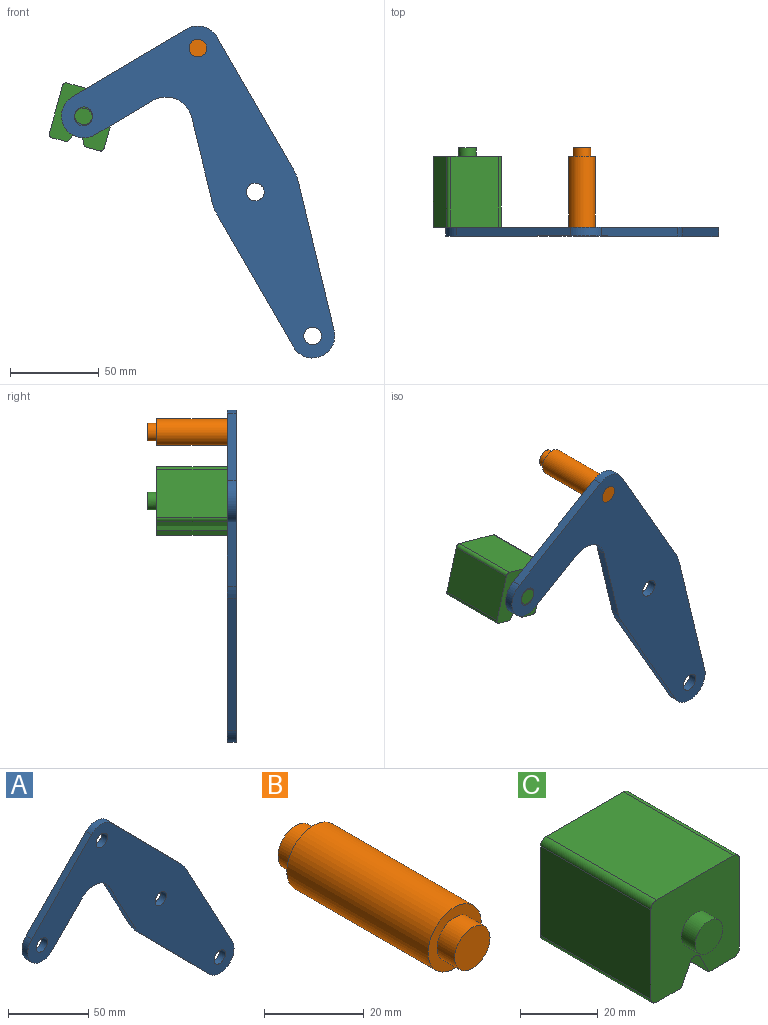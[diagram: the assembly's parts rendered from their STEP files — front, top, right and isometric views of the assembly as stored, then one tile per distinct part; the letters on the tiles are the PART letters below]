
ASSEMBLY  parts=3 mates=1
PART A: 18 faces, bbox 181.7x5x165.8 mm
  f0: plane 43.49x23.35mm, normal (-0.88,0,-0.47), area 246.8mm2, adj f1,f14,f16,f17
  f1: cylinder r=25mm len=5.75mm, axis (0,1,0), area 35.8mm2, adj f0,f2,f16,f17
  f2: plane 61.6x60.87mm, normal (-0.71,0,-0.7), area 433mm2, adj f1,f3,f16,f17
  f3: cylinder r=12.5mm len=21.39mm, axis (0,1,0), area 178.4mm2, adj f2,f4,f16,f17
  f4: plane 76.3x40.96mm, normal (0.88,0,0.47), area 433mm2, adj f3,f5,f16,f17
  f5: cylinder r=25mm len=5.75mm, axis (0,1,0), area 35.8mm2, adj f4,f6,f16,f17
  f6: plane 61.6x60.87mm, normal (0.71,0,0.7), area 433mm2, adj f5,f7,f16,f17
  f7: cylinder r=12.5mm len=17.78mm, axis (0,1,0), area 98.9mm2, adj f6,f8,f16,f17
  f8: plane 53.35x52.71mm, normal (-0.71,0,0.7), area 375mm2, adj f7,f9,f16,f17
  f9: cylinder r=12.5mm len=21.39mm, axis (0,1,0), area 196.3mm2, adj f8,f10,f16,f17
  f10: plane 26.86x26.54mm, normal (0.71,0,-0.7), area 188.8mm2, adj f9,f14,f16,f17
  f11: cylinder r=5mm len=10mm, axis (0,1,0), area 157.1mm2, adj f16,f17
  f12: cylinder r=5mm len=10mm, axis (0,1,0), area 157.1mm2, adj f16,f17
  f13: cylinder r=5mm len=10mm, axis (0,1,0), area 157.1mm2, adj f16,f17
  f14: cylinder r=15mm len=23.89mm, axis (0,1,0), area 140.2mm2, adj f0,f10,f16,f17
  f15: cylinder r=5mm len=10mm, axis (0,1,0), area 157.1mm2, adj f16,f17
  f16: plane 181.66x165.78mm, normal (0,-1,0), area 8710.1mm2, adj f0,f1,f2,f3,f4,f5,f6,f7
  f17: plane 181.66x165.78mm, normal (0,1,0), area 8710.1mm2, adj f0,f1,f2,f3,f4,f5,f6,f7
PART B: 7 faces, bbox 15x50x15 mm
  f0: cylinder r=7.5mm len=40mm, axis (0,-1,0), area 1885mm2, adj f2,f5
  f1: cylinder r=5mm len=10mm, axis (0,1,0), area 157.1mm2, adj f2,f3
  f2: plane 15x15mm, normal (0,-1,0), area 98.2mm2, adj f0,f1
  f3: plane 10x10mm, normal (0,-1,0), area 78.5mm2, adj f1
  f4: cylinder r=5mm len=10mm, axis (0,-1,0), area 157.1mm2, adj f5,f6
  f5: plane 15x15mm, normal (0,1,0), area 98.2mm2, adj f0,f4
  f6: plane 10x10mm, normal (0,1,0), area 78.5mm2, adj f4
PART C: 18 faces, bbox 32.1x50x32.1 mm
  f0: plane 40x28.08mm, normal (1,0,0), area 1123.1mm2, adj f4,f10,f13,f14
  f1: plane 40x9.04mm, normal (0,0,-1), area 361.6mm2, adj f2,f4,f10,f14
  f2: plane 40x6.42mm, normal (-0.89,0,-0.45), area 287.2mm2, adj f1,f4,f10,f15
  f3: plane 40x6.42mm, normal (0.89,0,-0.45), area 287.2mm2, adj f4,f5,f10,f15
  f4: plane 32.08x32.08mm, normal (0,-1,0), area 900.6mm2, adj f0,f1,f2,f3,f5,f6,f7,f9
  f5: plane 40x9.04mm, normal (0,0,-1), area 361.6mm2, adj f3,f4,f10,f16
  f6: plane 40x28.08mm, normal (0,0,1), area 1123.1mm2, adj f4,f10,f13,f17
  f7: plane 40x28.08mm, normal (-1,0,0), area 1123.1mm2, adj f4,f10,f16,f17
  f8: plane 10x10mm, normal (0,-1,0), area 78.5mm2, adj f9
  f9: cylinder r=5mm len=10mm, axis (0,1,0), area 157.1mm2, adj f4,f8
  f10: plane 32.08x32.08mm, normal (0,1,0), area 900.6mm2, adj f0,f1,f2,f3,f5,f6,f7,f12
  f11: plane 10x10mm, normal (0,1,0), area 78.5mm2, adj f12
  f12: cylinder r=5mm len=10mm, axis (0,-1,0), area 157.1mm2, adj f10,f11
  f13: cylinder r=2mm len=40mm, axis (0,1,0), area 125.7mm2, adj f0,f4,f6,f10
  f14: cylinder r=2mm len=40mm, axis (0,-1,0), area 125.7mm2, adj f0,f1,f4,f10
  f15: cylinder r=2mm len=40mm, axis (0,1,0), area 177.1mm2, adj f2,f3,f4,f10
  f16: cylinder r=2mm len=40mm, axis (0,1,0), area 125.7mm2, adj f4,f5,f7,f10
  f17: cylinder r=2mm len=40mm, axis (0,-1,0), area 125.7mm2, adj f4,f6,f7,f10
PLACE A rot(axis=(0,1,0),14.7deg) t=(0,-20,0)mm
PLACE B rot(axis=(0,1,0),14.7deg) t=(0,-20,0)mm
PLACE C rot(axis=(0,1,0),15.4deg) t=(-0.68,-20,-1.76)mm
MATE revolute C.f4 <-> A.f9  axis (0,-1,0) through (-96.93,-20,43.05)mm
